# Revit family: Skylight-Velux-Dynamic_Dome-CD1
name_source: partatom
category: Windows
revit_build: Autodesk Revit 2015 (Build: 20140606_1530(x64)
units: mm (PartAtom-declared; Revit-internal decimal feet)

## types (18) — shared parameters
Analytic Construction = <None>
Assembly Code = B3020110
BIMobject category = Skylights
BIMobject category code = windows-skylights
BIMobject main category = Windows
BIMobject main category code = windows
Brand url = http://www.veluxusa.com
Curb Material = Metal - Velux - Aluminum or Steel Curbs - Options for Application Preferences
Default Elevation = 0' - 0"
Description = Dynamic Dome Skylight
Design country = United States
Dome Material = Acrylic or Polycarbonate - Velux - Clear Impact Modified
Edition number = 1
Frame Material = Metal - Velux - Extruded Aluminum
Gasket Material = Rubber - Velux
IFC Classification = Sanitary Terminal
Manufacturer = VELUX
Manufacturer name = VELUX US
Masterformat 2014 Code = 08 62 13
Masterformat 2014 Description = Domed Unit Skylights
Nominal height = 0' - 0"
Nominal width = 0' - 0"
OmniClass Code = 23-17 17 13 11
OmniClass Description = Domed Unit Skylights
Performance Data = http://www.veluxusa.com
Product Documentation Link = http://www.veluxusa.com
Product Guid = 115938f8-e3be-4eea-ba24-74f30ed37992
Product Page URL = http://www.veluxusa.com
Product SKU = velux-dynamic-dome
Product certification = http://www.veluxusa.com
Product data url = https://bimobject.com
Product family = Windows
Product group = Skylights
Product url = http://www.veluxusa.com
QR code = http://bimobject.com
UNSPSC Code = 301718
URL = http://www.veluxusa.com
Uniclass 1.4 Code = L4145
Uniclass 1.4 Description = Skylights
Uniclass 2015 Code = Pr_30_59_72_77
Uniclass 2015 Name = Skylights
Weight Net (Kg) = 0

## per-type parameters (varying)
| type | Height | Length | Model | Outside Skylight Length | Outside Skylight Width | Rough Height | Rough Width | Width |
| 2496 | 1' - 5 1/8" | 8' - 0" | CD1 2496 | 8' - 5 27/32" | 2' - 5 27/32" | 1' - 5 1/8" | 2' - 0" | 2' - 0" |
| 2448 | 1' - 5 1/8" | 4' - 0" | CD1 2448 | 4' - 5 27/32" | 2' - 5 27/32" | 1' - 5 1/8" | 2' - 0" | 2' - 0" |
| 2412 | 1' - 5 1/8" | 10' - 0" | CD1 2412 | 10' - 5 27/32" | 2' - 5 27/32" | 1' - 5 1/8" | 2' - 0" | 2' - 0" |
| 3636 | 1' - 8 7/8" | 3' - 0" | CD1 3636 | 3' - 5 27/32" | 3' - 5 27/32" | 1' - 8 7/8" | 3' - 0" | 3' - 0" |
| 3660 | 1' - 8 7/8" | 5' - 0" | CD1 3660 | 5' - 5 27/32" | 3' - 5 27/32" | 1' - 8 7/8" | 3' - 0" | 3' - 0" |
| 3672 | 1' - 8 7/8" | 6' - 0" | CD1 3672 | 6' - 5 27/32" | 3' - 5 27/32" | 1' - 8 7/8" | 3' - 0" | 3' - 0" |
| 3696 | 1' - 8 7/8" | 8' - 0" | CD1 3696 | 8' - 5 27/32" | 3' - 5 27/32" | 1' - 8 7/8" | 3' - 0" | 3' - 0" |
| 3612 | 1' - 8 7/8" | 10' - 0" | CD1 3612 | 10' - 5 27/32" | 3' - 5 27/32" | 1' - 8 7/8" | 3' - 0" | 3' - 0" |
| 4848 | 2' - 0 1/2" | 4' - 0" | CD1 4848 | 4' - 5 27/32" | 4' - 5 27/32" | 2' - 0 1/2" | 4' - 0" | 4' - 0" |
| 4860 | 2' - 0 1/2" | 5' - 0" | CD1 4860 | 5' - 5 27/32" | 4' - 5 27/32" | 2' - 0 1/2" | 4' - 0" | 4' - 0" |
| 4872 | 2' - 0 1/2" | 6' - 0" | CD1 4872 | 6' - 5 27/32" | 4' - 5 27/32" | 2' - 0 1/2" | 4' - 0" | 4' - 0" |
| 4896 | 2' - 0 1/2" | 8' - 0" | CD1 4896 | 8' - 5 27/32" | 4' - 5 27/32" | 2' - 0 1/2" | 4' - 0" | 4' - 0" |
| 4812 | 2' - 0 1/2" | 10' - 0" | CD1 4812 | 10' - 5 27/32" | 4' - 5 27/32" | 2' - 0 1/2" | 4' - 0" | 4' - 0" |
| 6060 | 2' - 4 3/8" | 5' - 0" | CD1 6060 | 5' - 5 27/32" | 5' - 5 27/32" | 2' - 4 3/8" | 5' - 0" | 5' - 0" |
| 6072 | 2' - 4 3/8" | 6' - 0" | CD1 6072 | 6' - 5 27/32" | 5' - 5 27/32" | 2' - 4 3/8" | 5' - 0" | 5' - 0" |
| 6096 | 2' - 4 3/8" | 8' - 0" | CD1 6096 | 8' - 5 27/32" | 5' - 5 27/32" | 2' - 4 3/8" | 5' - 0" | 5' - 0" |
| 6012 | 2' - 4 3/8" | 10' - 0" | CD1 6012 | 10' - 5 27/32" | 5' - 5 27/32" | 2' - 4 3/8" | 5' - 0" | 5' - 0" |
| 7272 | 3' - 2 7/8" | 6' - 0" | CD1 7272 | 6' - 5 27/32" | 6' - 5 27/32" | 3' - 2 7/8" | 6' - 0" | 6' - 0" |

## geometry (parser evidence)
native form markers: Sweep x16
no freeform markers — native parametric forms only
